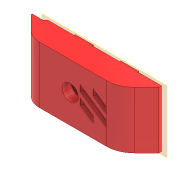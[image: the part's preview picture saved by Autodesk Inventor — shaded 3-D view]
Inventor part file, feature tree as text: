
AUTODESK INVENTOR PART (.ipt)
format: ipt  version: 2021 (Build 250183000, 183)  size: 279,552 bytes
history: native  units: mm
features: sketch x6, reference x6, extrude x5, other x3, chamfer x2, fillet x2, projected_geometry x2, plane x1, direct_edit x1, hole x1, delete_face x1, move_body x1
ambient origin geometry x8: Origin, YZ Plane, XZ Plane, XY Plane, X Axis, Y Axis, Z Axis, Center Point
bodies: Volumenkörper1 (feature_tree)
feature tree (31):
  extrude  "Extrusion1"  Depth=6.4mm
  plane  "Arbeitsebene1"
  extrude  "Extrusion2"  Depth=6.4mm
  chamfer  "Fase1"  Distance=6.4mm
  extrude  "Extrusion3"  Depth=6.4mm
  direct_edit  "Direktbearbeitung1"
  fillet  "Rundung1"  Radius=6.4mm
  extrude  "Extrusion4"  Depth=7.0mm
  hole  "Bohrung1"  [1 undecoded]
  chamfer  "Fase3"  Distance=0.1mm
  delete_face  "Fläche löschen1"
  extrude  "Extrusion7"  Depth=0.4mm TaperAngle=0.0deg
  fillet  "Rundung4"  Radius=0.1mm
  sketch  "Skizze1"  dims[d0=3.25mm d1=6.4mm]
  reference  "Referenz1"
  sketch  "Skizze2"  dims[d2=6.4mm d3=6.4mm]
  reference  "Referenz2"
  sketch  "Skizze3"  dims[d4=6.4mm]
  reference  "Referenz3"
  reference  "Referenz4"
  reference  "Referenz5"
  sketch  "Skizze4"  dims[d5=6.4mm]
  projected_geometry  "Projizierte Kontur1"
  sketch  "Skizze5"  dims[d6=5.0mm]
  projected_geometry  "Projizierte Kontur2"
  sketch  "Skizze8"  dims[d7=5.0mm d8=6.4mm d9=6.4mm d10=6.4mm d11=5.0mm d12=5.0mm d13=0.1mm d14=0.4mm d15=0.0mm d16=0.1mm d17=7.9mm d18=0.0mm d19=7.0mm d20=2.0mm d21=45.0deg d22=45.0deg d23=0.05mm d24=45.0deg d25=0.05mm d26=0.4mm d27=8.0mm d28=0.0mm d29=0.0mm d30=0.0mm d31=0.2mm d32=10.0mm d97=25.438174mm d99=2.2mm d102=1.913043mm d103=5.5mm d104=11.0mm d106=0.0mm d110=2.2mm d111=11.0mm d113=2.2mm d114=5.5mm d118=0.0mm d119=1.913043mm d124=9.092487mm d125=10.426087mm d126=25.215728mm d127=20.0mm d128=0.0mm d129=4.786957mm d130=1.0mm d131=0.0mm d135=25.215728mm d136=20.0mm d137=12.607864mm d138=10.0mm d139=3.2mm d140=6.0mm d141=5.6mm d142=3.2mm d143=90.0deg d144=8.0mm d145=20.594885mm d146=20.0mm d147=10.0mm d148=12.607864mm d149=5.6mm d150=0.8mm d151=2.0mm d152=45.0deg d167=0.0mm d168=0.4mm d169=0.0mm d170=0.0mm d171=7.0mm]
  reference  "Referenz13"
  other  "<userpath>\Desktop\Voron-2-2.4r1\Custom\Misumi GE5C\Gruppe.iam"
  other  "Gruppe.iam"
  other  "Z-Joint-Normal:1"
  move_body  "Verschieben1"
note: 1 required parameter value undecoded (feature->parameter linkage not recoverable at this tier; creation-order binding heuristic only, values carry confidence <= 0.55)
